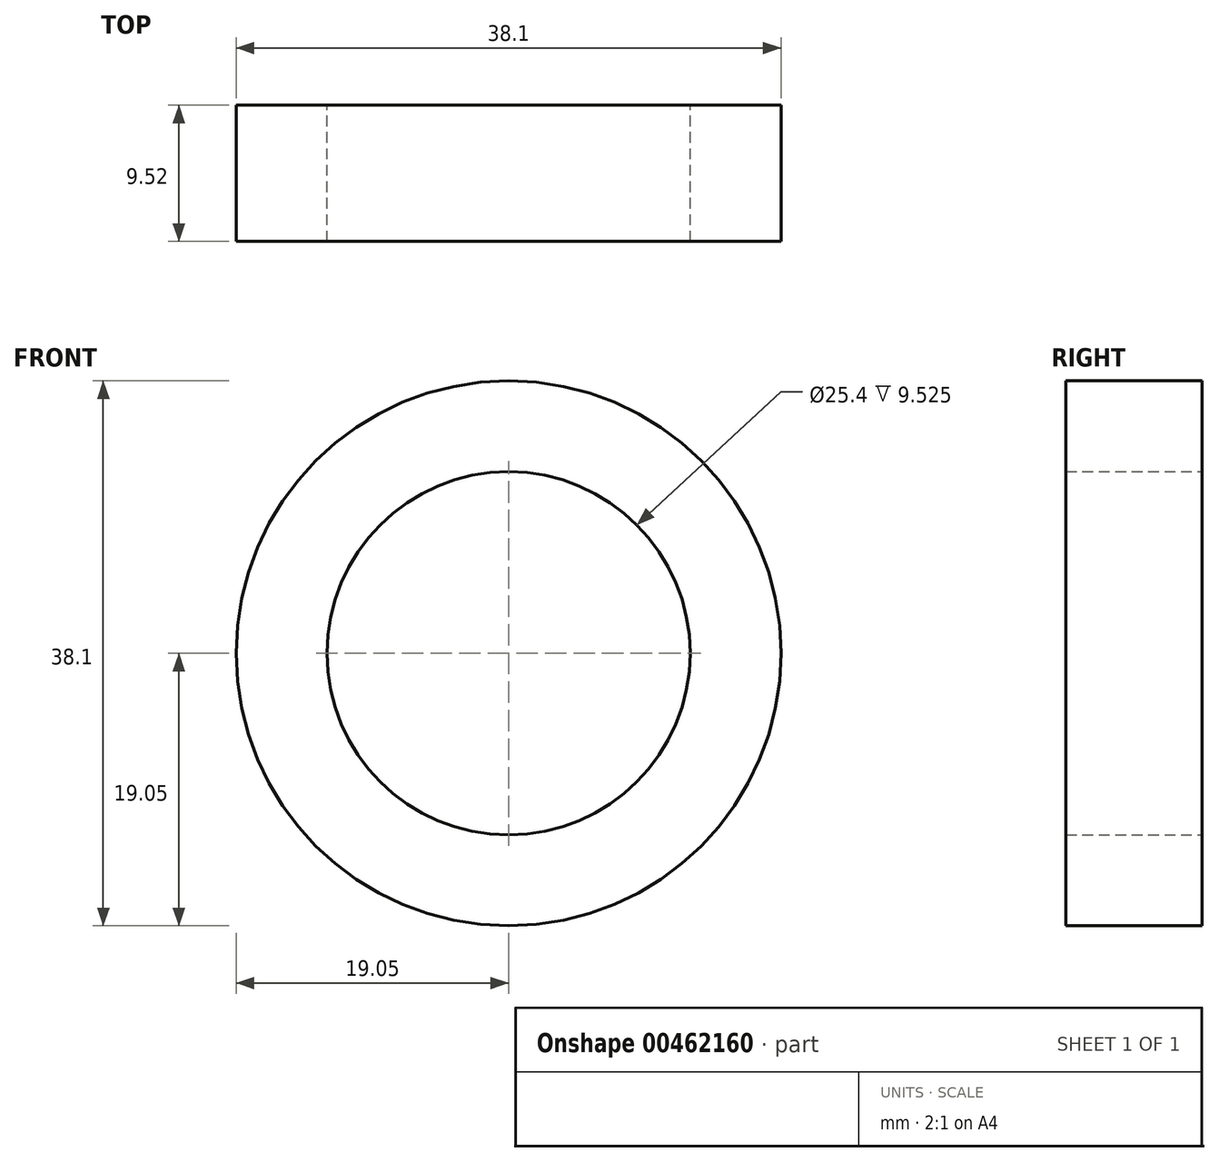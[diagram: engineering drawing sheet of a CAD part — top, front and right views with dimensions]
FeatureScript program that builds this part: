
annotation { "Feature Type Name" : "Feature", "Feature Type Description" : "" }
export const myFeature = defineFeature(function(context is Context, id is Id, definition is map)
    precondition{}
    {
        {
            var Q0;
            Q0=qCreatedBy(makeId("Front.planeOp"),FACE);
            var sketch = newSketch(context, id + "F0", { "sketchPlane" : qUnion([Q0])});
            skCircle(sketch, "E0", {"center": v(0, 0) * mm, "radius": 19.05 * mm});
            skCircle(sketch, "E1", {"center": v(0, 0) * mm, "radius": 12.7 * mm});
            skSolve(sketch);
        }
        {
            var Q0;
            Q0 = qSketchRegion(id + "F0", true);
            extrude(context, id + "F1", {"entities" : qUnion([Q0]), "depth" : 9.52 * mm, "symmetric" : true});
        }
    });
